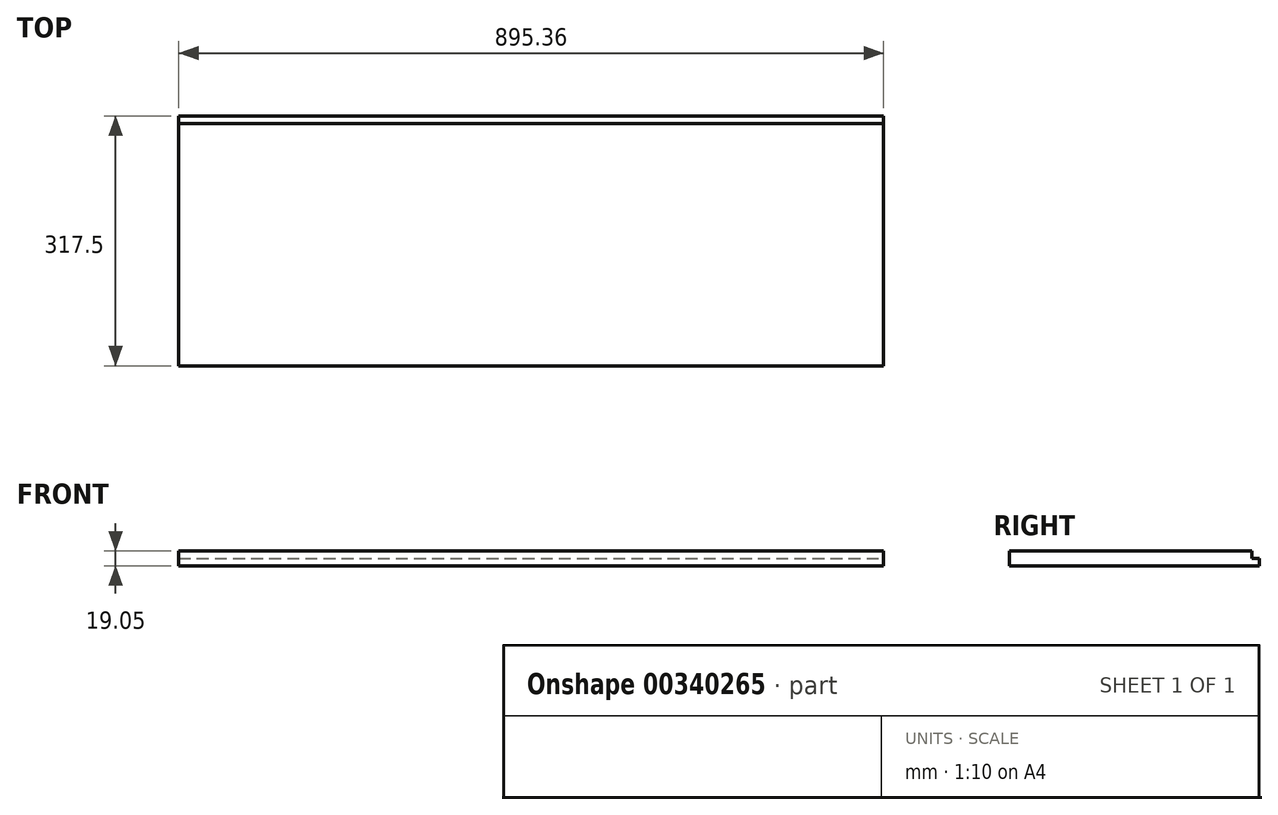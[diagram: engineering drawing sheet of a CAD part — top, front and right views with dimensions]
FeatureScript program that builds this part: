
annotation { "Feature Type Name" : "Feature", "Feature Type Description" : "" }
export const myFeature = defineFeature(function(context is Context, id is Id, definition is map)
    precondition{}
    {
        {
            var Q0;
            Q0=qCreatedBy(makeId("Top.planeOp"),FACE);
            var sketch = newSketch(context, id + "F0", { "sketchPlane" : qUnion([Q0])});
            skLineSegment(sketch, "E0.bottom", {"start": v(447.68, -158.75) * mm, "end": v(-447.68, -158.75) * mm});
            skLineSegment(sketch, "E0.top", {"start": v(447.68, 158.75) * mm, "end": v(-447.68, 158.75) * mm});
            skLineSegment(sketch, "E0.left", {"start": v(447.68, -158.75) * mm, "end": v(447.68, 158.75) * mm});
            skLineSegment(sketch, "E0.right", {"start": v(-447.68, -158.75) * mm, "end": v(-447.68, 158.75) * mm});
            skPoint(sketch, "E0.middle", {"position": v(0, 0) * mm});
            skSolve(sketch);
        }
        {
            var Q0;
            Q0 = qSketchRegion(id + "F0", true);
            extrude(context, id + "F1", {"entities" : qUnion([Q0]), "depth" : 19.05 * mm});
        }
        {
            var Q0;
            Q0=makeQuery(id+"F1.opExtrude","SWEPT_FACE",FACE,{"disambiguationData":[OSD([sQuery(id+"F0.wireOp",EDGE,"E0.left")])]});
            var sketch = newSketch(context, id + "F2", { "sketchPlane" : qUnion([Q0])});
            skLineSegment(sketch, "E1.bottom", {"start": v(149.23, 19.05) * mm, "end": v(158.75, 19.05) * mm});
            skLineSegment(sketch, "E1.top", {"start": v(149.23, 9.52) * mm, "end": v(158.75, 9.52) * mm});
            skLineSegment(sketch, "E1.left", {"start": v(149.23, 19.05) * mm, "end": v(149.23, 9.52) * mm});
            skLineSegment(sketch, "E1.right", {"start": v(158.75, 19.05) * mm, "end": v(158.75, 9.52) * mm});
            skSolve(sketch);
        }
        {
            var Q0;
            Q0 = qSketchRegion(id + "F2", true);
            extrude(context, id + "F3", {"entities" : qUnion([Q0]), "operationType" : NewBodyOperationType.REMOVE, "endBound" : BoundingType.THROUGH_ALL, "oppositeDirection" : true, "depth" : 25.4 * mm});
        }
    });
